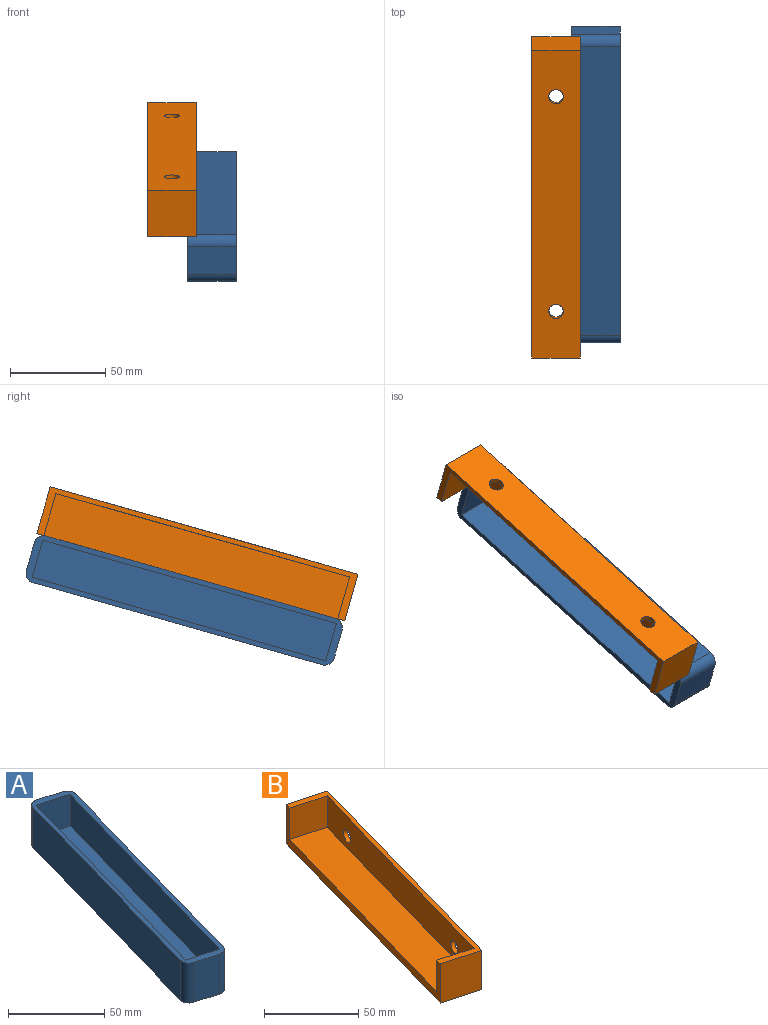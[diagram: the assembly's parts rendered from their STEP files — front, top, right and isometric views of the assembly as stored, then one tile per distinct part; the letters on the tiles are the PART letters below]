
ASSEMBLY  parts=2 mates=1
PART A: 15 faces, bbox 67.8x165.8x25.4 mm
  f0: plane 25.4x14.66mm, normal (0.27,0.96,0), area 387.1mm2, adj f8,f9,f11,f12
  f1: plane 151.49x43.02mm, normal (-0.96,0.27,0), area 4000mm2, adj f8,f9,f11,f13
  f2: plane 25.4x14.66mm, normal (-0.27,-0.96,0), area 387.1mm2, adj f8,f9,f13,f14
  f3: plane 153.93x43.71mm, normal (0.96,-0.27,0), area 3251.5mm2, adj f4,f6,f8,f10
  f4: plane 20.32x19.55mm, normal (-0.27,-0.96,0), area 412.9mm2, adj f3,f5,f8,f10
  f5: plane 153.93x43.71mm, normal (-0.96,0.27,0), area 3251.5mm2, adj f4,f6,f8,f10
  f6: plane 20.32x19.55mm, normal (0.27,0.96,0), area 412.9mm2, adj f3,f5,f8,f10
  f7: plane 151.49x43.02mm, normal (0.96,-0.27,0), area 4000mm2, adj f8,f9,f12,f14
  f8: plane 165.81x67.84mm, normal (0,0,1), area 984.4mm2, adj f0,f1,f2,f3,f4,f5,f6,f7
  f9: plane 165.81x67.84mm, normal (0,0,-1), area 4235.9mm2, adj f0,f1,f2,f7,f11,f12,f13,f14
  f10: plane 159.48x63.26mm, normal (0,0,1), area 3251.5mm2, adj f3,f4,f5,f6
  f11: cylinder r=5.08mm len=25.4mm, axis (0,0,-1), area 202.7mm2, adj f0,f1,f8,f9
  f12: cylinder r=5.08mm len=25.4mm, axis (0,0,-1), area 202.7mm2, adj f0,f7,f8,f9
  f13: cylinder r=5.08mm len=25.4mm, axis (0,0,-1), area 202.7mm2, adj f1,f2,f8,f9
  f14: cylinder r=5.08mm len=25.4mm, axis (0,0,-1), area 202.7mm2, adj f2,f7,f8,f9
PART B: 12 faces, bbox 70.2x168.2x25.4 mm
  f0: plane 21.99x20.32mm, normal (0.27,0.96,0), area 464.5mm2, adj f2,f3,f7,f9
  f1: plane 21.99x20.32mm, normal (-0.27,-0.96,0), area 464.5mm2, adj f2,f3,f7,f9
  f2: plane 153.93x43.71mm, normal (-0.96,0.27,0), area 3160.3mm2, adj f0,f1,f7,f9,f10,f11
  f3: plane 161.26x45.79mm, normal (-0.96,0.27,0), area 1006.6mm2, adj f0,f1,f4,f6,f7,f8,f9
  f4: plane 25.4x24.43mm, normal (-0.27,-0.96,0), area 645.2mm2, adj f3,f5,f7,f8
  f5: plane 161.26x45.79mm, normal (0.96,-0.27,0), area 4166.8mm2, adj f4,f6,f7,f8,f10,f11
  f6: plane 25.4x24.43mm, normal (0.27,0.96,0), area 645.2mm2, adj f3,f5,f7,f8
  f7: plane 168.2x70.23mm, normal (0,0,1), area 600.2mm2, adj f0,f1,f2,f3,f4,f5,f6
  f8: plane 168.2x70.23mm, normal (0,0,-1), area 4258.1mm2, adj f3,f4,f5,f6
  f9: plane 160.17x65.7mm, normal (0,0,1), area 3657.9mm2, adj f0,f1,f2,f3
  f10: cylinder r=3.81mm len=8.02mm, axis (0.96,-0.27,0), area 60.8mm2, adj f2,f5
  f11: cylinder r=3.81mm len=8.02mm, axis (0.96,-0.27,0), area 60.8mm2, adj f2,f5
PLACE A rot(axis=(0,-1,0),90deg) t=(100.19,-2.61,-17.95)mm
PLACE B rot(axis=(0,-1,0),90deg) t=(79.29,-9.55,6.49)mm
MATE fastened B.f3 <-> A.f7  axis (0,0.27,-0.96) through (74.79,-9.37,-20.75)mm
